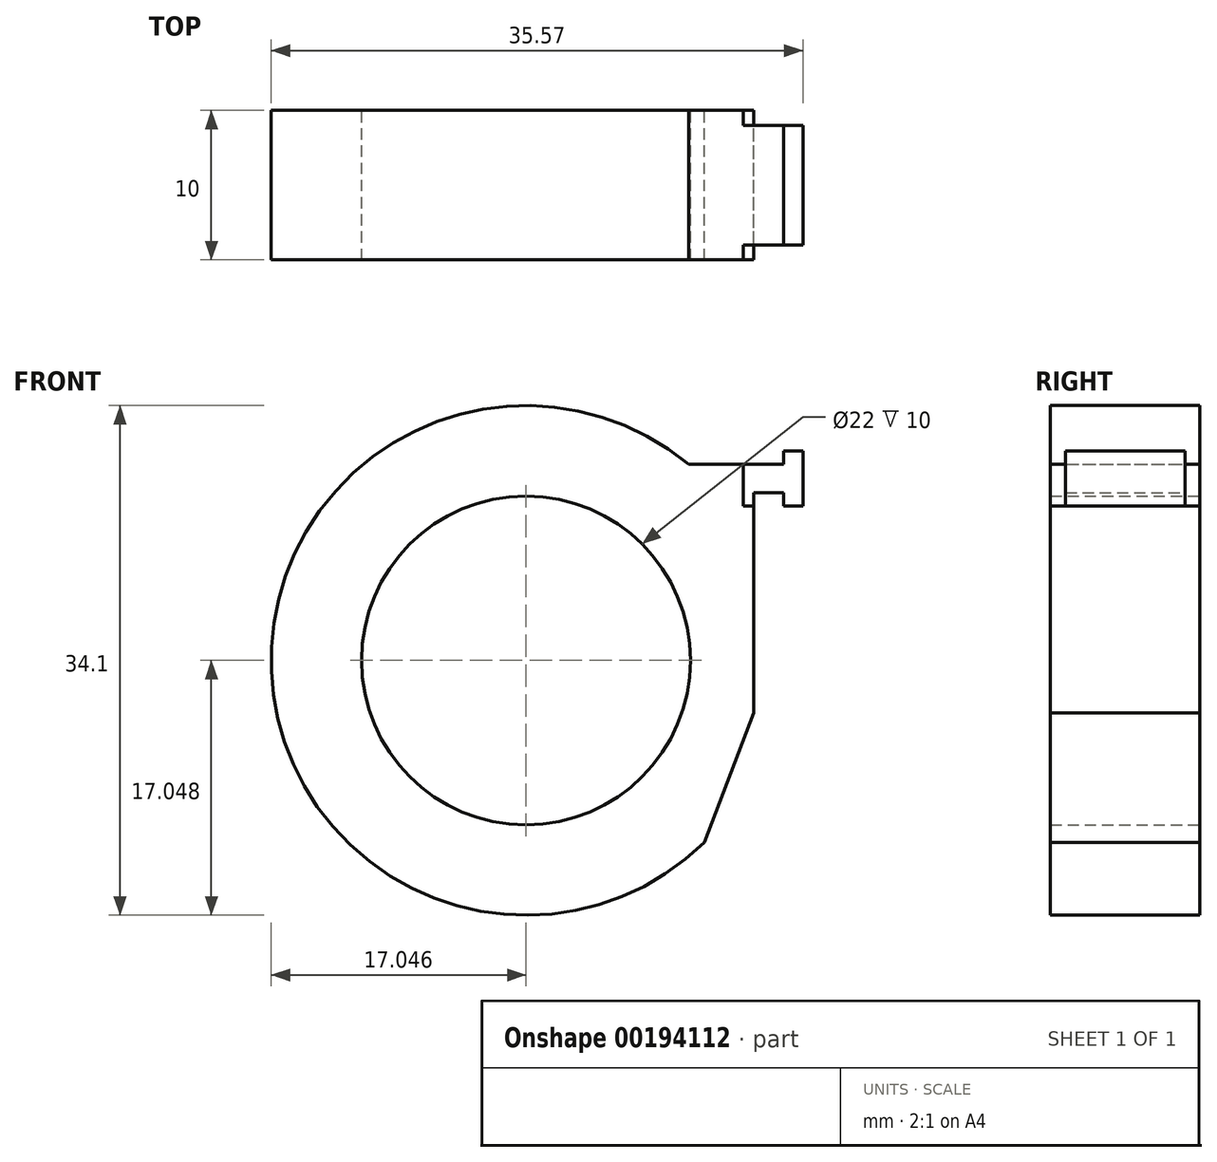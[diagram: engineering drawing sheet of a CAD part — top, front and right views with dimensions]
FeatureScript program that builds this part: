
annotation { "Feature Type Name" : "Feature", "Feature Type Description" : "" }
export const myFeature = defineFeature(function(context is Context, id is Id, definition is map)
    precondition{}
    {
        {
            var Q0;
            Q0=qCreatedBy(makeId("Front.planeOp"),FACE);
            var sketch = newSketch(context, id + "F0", { "sketchPlane" : qUnion([Q0])});
            skArc(sketch, "E0", {"start": v(-7.4, 9.89) * mm, "mid": v(-35.33, -3.94) * mm, "end": v(-6.35, -15.4) * mm});
            skCircle(sketch, "E1", {"center": v(-18.3, -3.23) * mm, "radius": 11 * mm});
            skLineSegment(sketch, "E2.right", {"start": v(-3.06, 3.98) * mm, "end": v(-3.06, -6.74) * mm});
            skLineSegment(sketch, "E3.left", {"start": v(0.23, 10.78) * mm, "end": v(0.23, 7.1) * mm});
            skLineSegment(sketch, "E4.bottom", {"start": v(-1.06, 10.78) * mm, "end": v(0.23, 10.78) * mm});
            skLineSegment(sketch, "E4.top", {"start": v(-1.06, 7.1) * mm, "end": v(0.23, 7.1) * mm});
            skLineSegment(sketch, "E4.left", {"start": v(-1.06, 10.78) * mm, "end": v(-1.06, 9.89) * mm});
            skPoint(sketch, "E4.middle", {"position": v(0.23, 8.94) * mm});
            skPoint(sketch, "E4.right.end.orphan", {"position": v(1.52, 7.1) * mm});
            skPoint(sketch, "E4.right.start.orphan", {"position": v(1.52, 10.78) * mm});
            skLineSegment(sketch, "E5.bottom", {"start": v(-3.06, 9.89) * mm, "end": v(-1.06, 9.89) * mm});
            skLineSegment(sketch, "E5.top", {"start": v(-3.06, 7.99) * mm, "end": v(-1.06, 7.99) * mm});
            skLineSegment(sketch, "E5.left", {"start": v(-3.06, 9.89) * mm, "end": v(-3.06, 7.99) * mm});
            skPoint(sketch, "E5.cornerSnap0", {"position": v(-3.06, 8.94) * mm});
            skPoint(sketch, "E6.orphan", {"position": v(0.23, 15.97) * mm});
            skPoint(sketch, "E5.right.start.orphan", {"position": v(3.52, 9.89) * mm});
            skPoint(sketch, "E7.orphan", {"position": v(3.52, 7.99) * mm});
            skPoint(sketch, "E8.orphan", {"position": v(0.23, 33.26) * mm});
            skLineSegment(sketch, "E9", {"start": v(-3.06, 9.89) * mm, "end": v(-7.4, 9.89) * mm});
            skLineSegment(sketch, "E10", {"start": v(-3.06, 7.99) * mm, "end": v(-3.06, 3.98) * mm});
            skPoint(sketch, "E11.orphan", {"position": v(-6.35, 8.94) * mm});
            skPoint(sketch, "E12", {"position": v(-1.06, 9.89) * mm});
            skPoint(sketch, "E13", {"position": v(-1.06, 7.99) * mm});
            skLineSegment(sketch, "E14.trimOffspring", {"start": v(-1.06, 7.99) * mm, "end": v(-1.06, 7.1) * mm});
            skLineSegment(sketch, "E15", {"start": v(-3.06, -6.74) * mm, "end": v(-6.35, -15.4) * mm});
            skPoint(sketch, "E16", {"position": v(-9.03, -9.16) * mm});
            skPoint(sketch, "E17", {"position": v(-7.87, -6.74) * mm});
            skSolve(sketch);
        }
        {
            var Q0;
            Q0 = qSketchRegion(id + "F0", true);
            extrude(context, id + "F1", {"entities" : qUnion([Q0]), "depth" : 10 * mm});
        }
        {
            var Q0;
            Q0=makeQuery(id+"F1.opExtrude","SWEPT_FACE",FACE,{"disambiguationData":[OSD([sQuery(id+"F0.wireOp",EDGE,"E3.left")])]});
            var sketch = newSketch(context, id + "F2", { "sketchPlane" : qUnion([Q0])});
            skLineSegment(sketch, "E18", {"start": v(-5, 10.78) * mm, "end": v(-5, 7.1) * mm});
            skLineSegment(sketch, "E19.left", {"start": v(-1, 7.1) * mm, "end": v(-1, 10.78) * mm});
            skLineSegment(sketch, "E19.right", {"start": v(-9, 7.1) * mm, "end": v(-9, 10.78) * mm});
            skPoint(sketch, "E19.middle", {"position": v(-5, 10.78) * mm});
            skPoint(sketch, "E20", {"position": v(-9, 10.78) * mm});
            skPoint(sketch, "E21", {"position": v(-9, 7.1) * mm});
            skPoint(sketch, "E22", {"position": v(-1, 10.78) * mm});
            skPoint(sketch, "E23", {"position": v(-1, 7.1) * mm});
            skPoint(sketch, "E24.orphan", {"position": v(-9, 6.09) * mm});
            skPoint(sketch, "E25.orphan", {"position": v(-1, 6.09) * mm});
            skPoint(sketch, "E26.orphan", {"position": v(-1, 15.48) * mm});
            skPoint(sketch, "E27.orphan", {"position": v(-9, 15.48) * mm});
            skSolve(sketch);
        }
        {
            var Q0;
            Q0 = qSketchRegion(id + "F2", true);
            var Q1;
            {var subQ0=sQuery(id+"F2.wireOp",EDGE,"E19.right");Q1=makeQuery(id+"F2.imprint","IMPRINT",FACE,{"disambiguationData":[TD([[makeQuery(id+"F2.imprint","IMPRINT",EDGE,{"derivedFrom":subQ0}),1.0]])]});}
            var Q2;
            {var subQ0=sQuery(id+"F2.wireOp",EDGE,"E19.left");Q2=makeQuery(id+"F2.imprint","IMPRINT",FACE,{"disambiguationData":[TD([[makeQuery(id+"F2.imprint","IMPRINT",EDGE,{"derivedFrom":subQ0}),-1.0]])]});}
            extrude(context, id + "F3", {"entities" : qUnion([Q0, Q1, Q2]), "operationType" : NewBodyOperationType.REMOVE, "oppositeDirection" : true, "depth" : 4 * mm});
        }
    });
